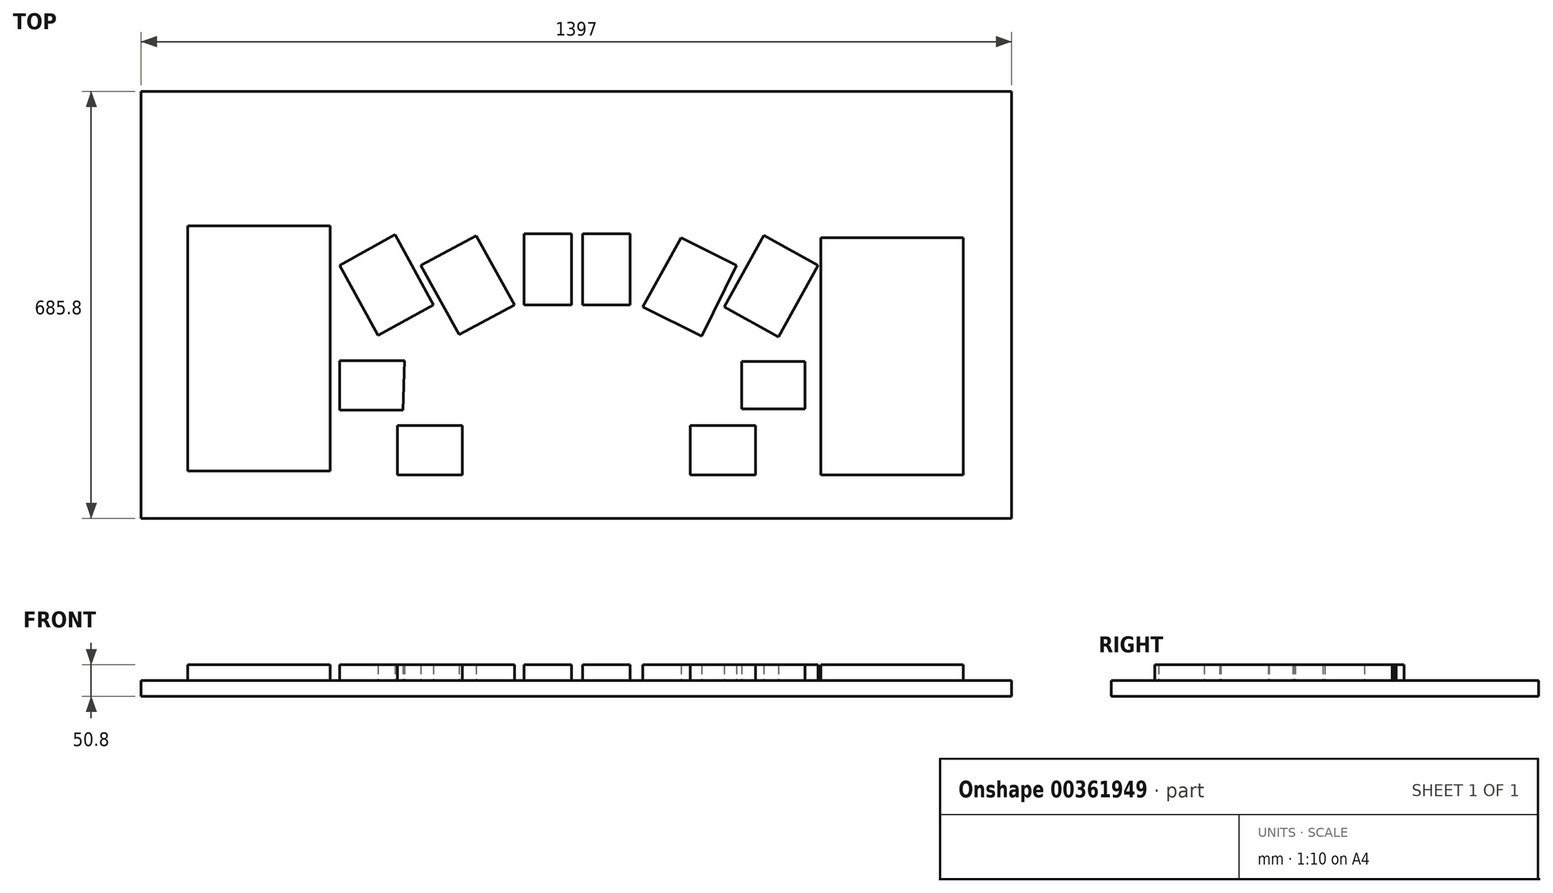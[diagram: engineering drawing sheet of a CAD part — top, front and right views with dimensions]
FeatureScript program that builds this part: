
annotation { "Feature Type Name" : "Feature", "Feature Type Description" : "" }
export const myFeature = defineFeature(function(context is Context, id is Id, definition is map)
    precondition{}
    {
        {
            var Q0;
            Q0=qCreatedBy(makeId("Top.planeOp"),FACE);
            var sketch = newSketch(context, id + "F0", { "sketchPlane" : qUnion([Q0])});
            skLineSegment(sketch, "E0.bottom", {"start": v(698.5, 342.9) * mm, "end": v(-698.5, 342.9) * mm});
            skLineSegment(sketch, "E0.top", {"start": v(698.5, -342.9) * mm, "end": v(-698.5, -342.9) * mm});
            skLineSegment(sketch, "E0.left", {"start": v(698.5, 342.9) * mm, "end": v(698.5, -342.9) * mm});
            skLineSegment(sketch, "E0.right", {"start": v(-698.5, 342.9) * mm, "end": v(-698.5, -342.9) * mm});
            skPoint(sketch, "E0.middle", {"position": v(0, 0) * mm});
            skSolve(sketch);
        }
        {
            var Q0;
            Q0=qSketchRegion(id+"F0",true);
            extrude(context, id + "F1", {"entities" : qUnion([Q0]), "depth" : 25.4 * mm});
        }
        {
            var Q0;
            Q0=makeQuery(id+"F1.opExtrude","CAP_FACE",FACE,{"disambiguationData":[OSD([sQuery(id+"F0.wireOp",EDGE,"E0.bottom"),sQuery(id+"F0.wireOp",EDGE,"E0.top"),sQuery(id+"F0.wireOp",EDGE,"E0.left"),sQuery(id+"F0.wireOp",EDGE,"E0.right")])],"isStart":false});
            var sketch = newSketch(context, id + "F2", { "sketchPlane" : qUnion([Q0])});
            skLineSegment(sketch, "E1.bottom", {"start": v(190.5, -143.2) * mm, "end": v(-190.5, -143.2) * mm, "construction": true});
            skLineSegment(sketch, "E1.top", {"start": v(190.5, -67) * mm, "end": v(-190.5, -67) * mm, "construction": true});
            skLineSegment(sketch, "E1.left", {"start": v(190.5, -143.2) * mm, "end": v(190.5, -67) * mm, "construction": true});
            skLineSegment(sketch, "E1.right", {"start": v(-190.5, -143.2) * mm, "end": v(-190.5, -67) * mm, "construction": true});
            skPoint(sketch, "E1.middle", {"position": v(0, -105.1) * mm});
            skPoint(sketch, "E2", {"position": v(199.74, -67) * mm});
            skPoint(sketch, "E3.positionSnap0", {"position": v(190.5, -105.1) * mm});
            skPoint(sketch, "E4", {"position": v(-394.97, 127) * mm});
            skLineSegment(sketch, "E5.bottom", {"start": v(-394.97, 127) * mm, "end": v(-623.57, 127) * mm});
            skLineSegment(sketch, "E5.top", {"start": v(-394.97, -266.7) * mm, "end": v(-623.57, -266.7) * mm});
            skLineSegment(sketch, "E5.left", {"start": v(-394.97, 127) * mm, "end": v(-394.97, -266.7) * mm});
            skLineSegment(sketch, "E5.right", {"start": v(-623.57, 127) * mm, "end": v(-623.57, -266.7) * mm});
            skLineSegment(sketch, "E6.bottom", {"start": v(392.43, 107.95) * mm, "end": v(621.03, 107.95) * mm});
            skLineSegment(sketch, "E6.top", {"start": v(392.43, -273.05) * mm, "end": v(621.03, -273.05) * mm});
            skLineSegment(sketch, "E6.left", {"start": v(392.43, 107.95) * mm, "end": v(392.43, -273.05) * mm});
            skLineSegment(sketch, "E6.right", {"start": v(621.03, 107.95) * mm, "end": v(621.03, -273.05) * mm});
            skLineSegment(sketch, "E7.top", {"start": v(182.88, -193.64) * mm, "end": v(287.37, -193.64) * mm});
            skLineSegment(sketch, "E7.left", {"start": v(182.88, -273.05) * mm, "end": v(182.88, -193.64) * mm});
            skLineSegment(sketch, "E7.right", {"start": v(287.37, -273.05) * mm, "end": v(287.37, -193.64) * mm});
            skLineSegment(sketch, "E8", {"start": v(182.88, -273.05) * mm, "end": v(287.37, -273.05) * mm});
            skLineSegment(sketch, "E9", {"start": v(106.68, -3.56) * mm, "end": v(200.97, -50.21) * mm});
            skLineSegment(sketch, "E10", {"start": v(200.97, -50.21) * mm, "end": v(257.22, 63.5) * mm});
            skLineSegment(sketch, "E11", {"start": v(257.22, 63.5) * mm, "end": v(168.16, 107.56) * mm});
            skLineSegment(sketch, "E12", {"start": v(168.16, 107.56) * mm, "end": v(106.68, -3.56) * mm});
            skLineSegment(sketch, "E13", {"start": v(237.3, -3.56) * mm, "end": v(324.04, -51.55) * mm});
            skLineSegment(sketch, "E14", {"start": v(324.04, -51.55) * mm, "end": v(387.7, 63.5) * mm});
            skLineSegment(sketch, "E15", {"start": v(387.7, 63.5) * mm, "end": v(300.96, 111.49) * mm});
            skLineSegment(sketch, "E16", {"start": v(300.96, 111.49) * mm, "end": v(237.3, -3.56) * mm});
            skPoint(sketch, "E17.endSnap0", {"position": v(0, 342.9) * mm});
            skLineSegment(sketch, "E18.MirrorCS", {"start": v(-160.54, 111.12) * mm, "end": v(-99.06, 0) * mm});
            skLineSegment(sketch, "E19.MirrorCS", {"start": v(-249.44, 63.5) * mm, "end": v(-160.54, 111.12) * mm});
            skLineSegment(sketch, "E20.MirrorCS", {"start": v(-99.06, 0) * mm, "end": v(-187.96, -47.63) * mm});
            skLineSegment(sketch, "E21.MirrorCS", {"start": v(-187.96, -47.63) * mm, "end": v(-249.44, 63.5) * mm});
            skLineSegment(sketch, "E22.MirrorCS", {"start": v(-291.17, 112.69) * mm, "end": v(-229.69, 0) * mm});
            skLineSegment(sketch, "E23.MirrorCS", {"start": v(-229.69, 0) * mm, "end": v(-318.59, -49.19) * mm});
            skLineSegment(sketch, "E24.MirrorCS", {"start": v(-318.59, -49.19) * mm, "end": v(-380.07, 63.5) * mm});
            skLineSegment(sketch, "E25.MirrorCS", {"start": v(-380.07, 63.5) * mm, "end": v(-291.17, 112.69) * mm});
            skPoint(sketch, "E26", {"position": v(153.82, -26.89) * mm});
            skPoint(sketch, "E27", {"position": v(-143.5, -23.81) * mm});
            skPoint(sketch, "E28", {"position": v(-274.14, -24.6) * mm});
            skPoint(sketch, "E29", {"position": v(280.67, -27.55) * mm});
            skPoint(sketch, "E30", {"position": v(-394.97, -69.85) * mm});
            skPoint(sketch, "E31", {"position": v(392.43, -82.55) * mm});
            skPoint(sketch, "E32", {"position": v(235.13, -233.35) * mm});
            skLineSegment(sketch, "E33.bottom", {"start": v(-83.82, 0) * mm, "end": v(-7.62, -0.14) * mm});
            skLineSegment(sketch, "E33.left", {"start": v(-83.82, 0) * mm, "end": v(-83.82, 114.16) * mm});
            skLineSegment(sketch, "E33.right", {"start": v(-7.62, -0.14) * mm, "end": v(-7.62, 114.16) * mm});
            skLineSegment(sketch, "E34", {"start": v(-7.62, 114.16) * mm, "end": v(-83.82, 114.16) * mm});
            skLineSegment(sketch, "E35.bottom", {"start": v(10.16, 0) * mm, "end": v(86.36, -0.14) * mm});
            skLineSegment(sketch, "E35.left", {"start": v(10.16, 0) * mm, "end": v(10.16, 114.16) * mm});
            skLineSegment(sketch, "E35.right", {"start": v(86.36, -0.14) * mm, "end": v(86.36, 114.16) * mm});
            skLineSegment(sketch, "E36", {"start": v(86.36, 114.16) * mm, "end": v(10.16, 114.16) * mm});
            skLineSegment(sketch, "E37.MirrorCS", {"start": v(-182.88, -273.05) * mm, "end": v(-182.88, -193.64) * mm});
            skLineSegment(sketch, "E38.MirrorCS", {"start": v(-182.88, -193.64) * mm, "end": v(-287.37, -193.64) * mm});
            skLineSegment(sketch, "E39.MirrorCS", {"start": v(-287.37, -273.05) * mm, "end": v(-287.37, -193.64) * mm});
            skPoint(sketch, "E40.MirrorP", {"position": v(-235.13, -233.35) * mm});
            skLineSegment(sketch, "E41.MirrorCS", {"start": v(-182.88, -273.05) * mm, "end": v(-287.37, -273.05) * mm});
            skLineSegment(sketch, "E42.MirrorCS", {"start": v(-275.58, -89.5) * mm, "end": v(-380.07, -89.5) * mm});
            skLineSegment(sketch, "E43.MirrorCS", {"start": v(-380.07, -168.91) * mm, "end": v(-380.07, -89.5) * mm});
            skPoint(sketch, "E44.MirrorP", {"position": v(-327.83, -129.2) * mm});
            skLineSegment(sketch, "E45.MirrorCS", {"start": v(-278.47, -168.91) * mm, "end": v(-380.07, -168.91) * mm});
            skLineSegment(sketch, "E46.bottom", {"start": v(366.63, -166.85) * mm, "end": v(265.03, -166.85) * mm});
            skLineSegment(sketch, "E46.top", {"start": v(366.63, -90.65) * mm, "end": v(265.03, -90.65) * mm});
            skLineSegment(sketch, "E46.left", {"start": v(366.63, -166.85) * mm, "end": v(366.63, -90.65) * mm});
            skLineSegment(sketch, "E46.right", {"start": v(265.03, -166.85) * mm, "end": v(265.03, -90.65) * mm});
            skLineSegment(sketch, "E47", {"start": v(-275.58, -89.5) * mm, "end": v(-278.47, -168.91) * mm});
            skSolve(sketch);
        }
        {
            var Q0;
            Q0=qSketchRegion(id+"F2",true);
            extrude(context, id + "F3", {"entities" : qUnion([Q0]), "depth" : 25.4 * mm});
        }
    });
